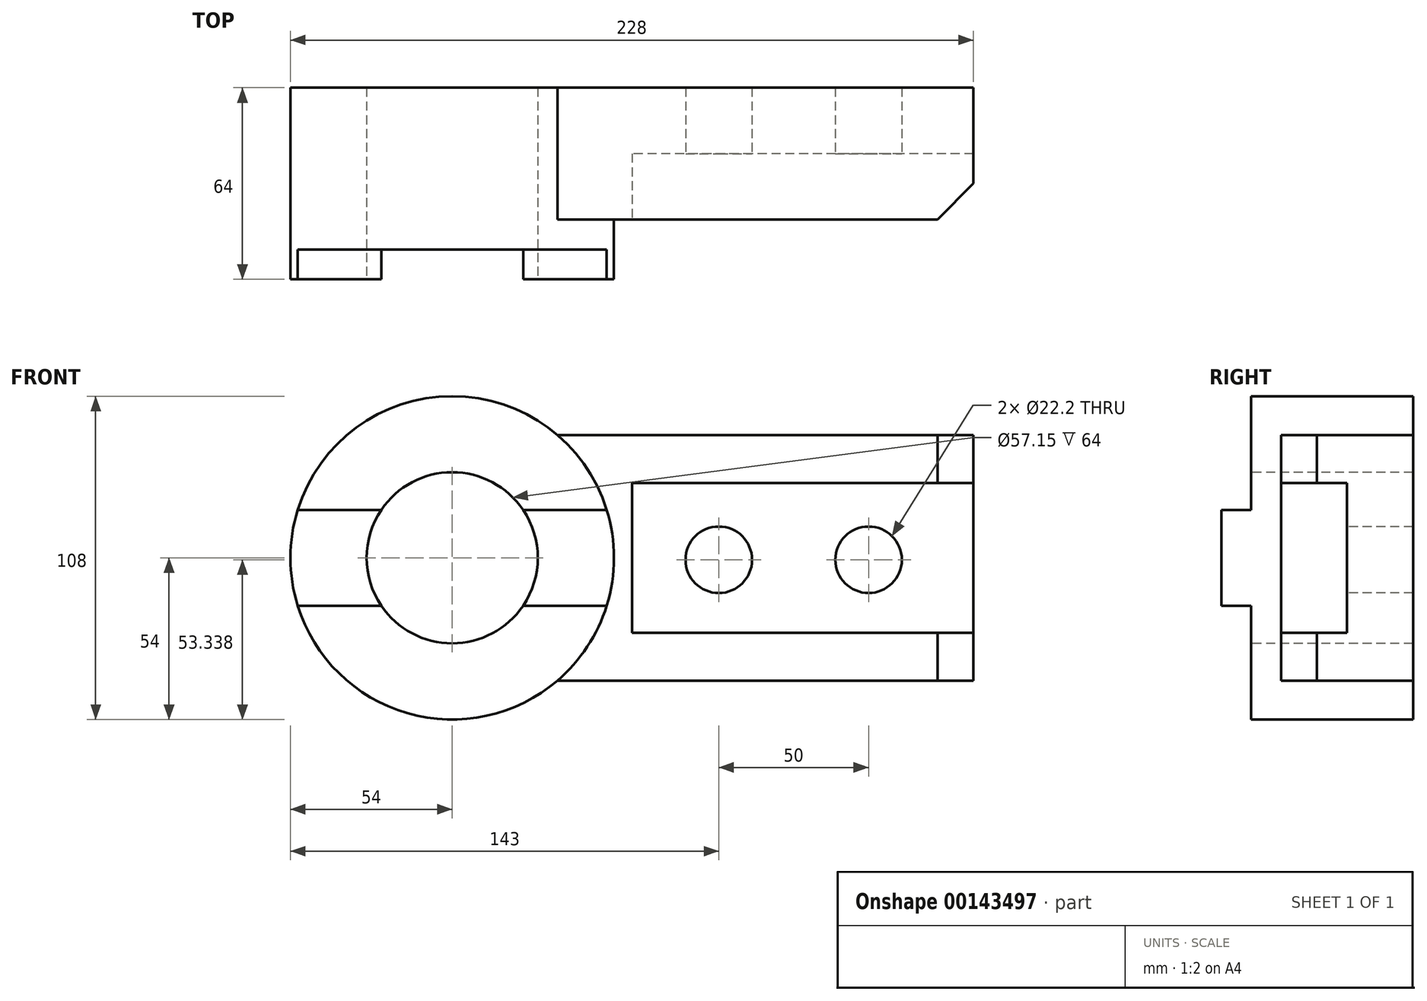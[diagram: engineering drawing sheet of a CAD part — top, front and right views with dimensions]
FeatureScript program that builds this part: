
annotation { "Feature Type Name" : "Feature", "Feature Type Description" : "" }
export const myFeature = defineFeature(function(context is Context, id is Id, definition is map)
    precondition{}
    {
        {
            var Q0;
            Q0=qCreatedBy(makeId("Front.planeOp"),FACE);
            var sketch = newSketch(context, id + "F0", { "sketchPlane" : qUnion([Q0])});
            skLineSegment(sketch, "E0.bottom", {"start": v(0, 0) * mm, "end": v(174, 0) * mm});
            skLineSegment(sketch, "E0.top", {"start": v(0, 82) * mm, "end": v(174, 82) * mm});
            skLineSegment(sketch, "E0.left", {"start": v(0, 0) * mm, "end": v(0, 82) * mm});
            skLineSegment(sketch, "E0.right", {"start": v(174, 0) * mm, "end": v(174, 82) * mm});
            skLineSegment(sketch, "E1.bottom", {"start": v(174, 66) * mm, "end": v(60, 66) * mm});
            skLineSegment(sketch, "E1.top", {"start": v(174, 16) * mm, "end": v(60, 16) * mm});
            skLineSegment(sketch, "E1.left", {"start": v(174, 66) * mm, "end": v(174, 16) * mm});
            skLineSegment(sketch, "E1.right", {"start": v(60, 66) * mm, "end": v(60, 16) * mm});
            skSolve(sketch);
        }
        {
            var Q0;
            {var subQ1=sQuery(id+"F0.wireOp",EDGE,"E0.bottom");Q0=makeQuery(id+"F0.imprint","IMPRINT",FACE,{"disambiguationData":[TD([[makeQuery(id+"F0.imprint","IMPRINT",EDGE,{"derivedFrom":subQ1}),1.0]])]});}
            var Q1;
            Q1=makeQuery(id+"F0.imprint","IMPRINT",FACE,{"disambiguationData":[TD([[makeQuery(id+"F0.imprint","IMPRINT",EDGE,{"derivedFrom":sQuery(id+"F0.wireOp",EDGE,"E1.bottom")}),1.0]])]});
            extrude(context, id + "F1", {"entities" : qUnion([Q0, Q1]), "oppositeDirection" : true, "depth" : 44 * mm});
        }
        {
            var Q0;
            Q0=makeQuery(id+"F0.imprint","IMPRINT",FACE,{"disambiguationData":[TD([[makeQuery(id+"F0.imprint","IMPRINT",EDGE,{"derivedFrom":sQuery(id+"F0.wireOp",EDGE,"E1.bottom")}),1.0]])]});
            extrude(context, id + "F2", {"entities" : qUnion([Q0]), "operationType" : NewBodyOperationType.REMOVE, "oppositeDirection" : true, "depth" : 22 * mm});
        }
        {
            var Q0;
            Q0=makeQuery(id+"F1.opExtrude","SWEPT_FACE",FACE,{"disambiguationData":[OSD([sQuery(id+"F0.wireOp",EDGE,"E0.top")])]});
            var sketch = newSketch(context, id + "F3", { "sketchPlane" : qUnion([Q0])});
            skLineSegment(sketch, "E2", {"start": v(174, 12) * mm, "end": v(162, 0) * mm});
            skLineSegment(sketch, "E3", {"start": v(162, 0) * mm, "end": v(174, 0) * mm});
            skLineSegment(sketch, "E4", {"start": v(174, 0) * mm, "end": v(174, 12) * mm});
            skSolve(sketch);
        }
        {
            var Q0;
            Q0 = qSketchRegion(id + "F3", true);
            extrude(context, id + "F4", {"entities" : qUnion([Q0]), "operationType" : NewBodyOperationType.REMOVE, "endBound" : BoundingType.THROUGH_ALL, "oppositeDirection" : true, "depth" : 25 * mm});
        }
        {
            var Q0;
            Q0=makeQuery(id+"F2.boolean.opBoolean","COPY",FACE,{"derivedFrom":makeQuery(id+"F2.opExtrude","CAP_FACE",FACE,{"disambiguationData":[OSD([sQuery(id+"F0.wireOp",EDGE,"E1.bottom"),sQuery(id+"F0.wireOp",EDGE,"E1.top"),sQuery(id+"F0.wireOp",EDGE,"E1.left"),sQuery(id+"F0.wireOp",EDGE,"E1.right")])],"isStart":false})});
            var sketch = newSketch(context, id + "F5", { "sketchPlane" : qUnion([Q0])});
            skPoint(sketch, "E5", {"position": v(89, 40.34) * mm});
            skPoint(sketch, "E6", {"position": v(139, 40.34) * mm});
            skSolve(sketch);
        }
        {
            var Q0;
            Q0=sQuery(id+"F5.wireOp",VERTEX,"E5");
            var Q1;
            Q1=sQuery(id+"F5.wireOp",VERTEX,"E6");
            var Q2;
            Q2=makeQuery(id+"F1.opExtrude","SWEPT_BODY",BODY,{"disambiguationData":[OSD([sQuery(id+"F0.wireOp",EDGE,"E0.bottom"),sQuery(id+"F0.wireOp",EDGE,"E0.top"),sQuery(id+"F0.wireOp",EDGE,"E0.left"),sQuery(id+"F0.wireOp",EDGE,"E0.right"),sQuery(id+"F0.wireOp",EDGE,"E1.left")])]});
            hole(context, id + "F6", {"style" : HoleStyle.SIMPLE, "endStyle" : HoleEndStyle.THROUGH, "holeDiameter" : 22.2 * mm, "locations" : qUnion([Q0, Q1]), "scope" : qUnion([Q2]), "isTappedThrough" : true});
        }
        {
            var Q0;
            Q0=qCreatedBy(makeId("Front.planeOp"),FACE);
            var sketch = newSketch(context, id + "F7", { "sketchPlane" : qUnion([Q0])});
            skLineSegment(sketch, "E7", {"start": v(0, 41) * mm, "end": v(181.48, 41) * mm, "construction": true});
            skLineSegment(sketch, "E8", {"start": v(0, 41) * mm, "end": v(0, 41) * mm});
            skCircle(sketch, "E9", {"center": v(0, 41) * mm, "radius": 54 * mm});
            skCircle(sketch, "E10", {"center": v(0, 41) * mm, "radius": 28.57 * mm});
            skSolve(sketch);
        }
        {
            var Q0;
            Q0=makeQuery(id+"F7.imprint","IMPRINT",FACE,{"disambiguationData":[TD([[makeQuery(id+"F7.imprint","IMPRINT",EDGE,{"derivedFrom":sQuery(id+"F7.wireOp",EDGE,"E9")}),1.0]])]});
            extrude(context, id + "F8", {"entities" : qUnion([Q0]), "operationType" : NewBodyOperationType.ADD, "oppositeDirection" : true, "depth" : 44 * mm, "hasSecondDirection" : true, "secondDirectionOppositeDirection" : false, "secondDirectionDepth" : 10 * mm});
        }
        {
            var Q0;
            {var subQ0=sQuery(id+"F0.wireOp",EDGE,"E0.left");Q0=makeQuery(id+"F8.boolean.opBoolean","SPLIT",FACE,{"disambiguationData":[TD([makeQuery(id+"F1.opExtrude","SWEPT_FACE",FACE,{"disambiguationData":[OSD([subQ0])]})])],"derivedFrom":makeQuery(id+"F1.opExtrude","CAP_FACE",FACE,{"disambiguationData":[OSD([sQuery(id+"F0.wireOp",EDGE,"E0.bottom"),sQuery(id+"F0.wireOp",EDGE,"E0.top"),subQ0,sQuery(id+"F0.wireOp",EDGE,"E0.right"),sQuery(id+"F0.wireOp",EDGE,"E1.left")])],"isStart":true})});}
            extrude(context, id + "F9", {"entities" : qUnion([Q0]), "operationType" : NewBodyOperationType.REMOVE, "endBound" : BoundingType.THROUGH_ALL, "oppositeDirection" : true, "depth" : 25 * mm});
        }
        {
            var Q0;
            Q0=makeQuery(id+"F8.opExtrude","CAP_FACE",FACE,{"disambiguationData":[OSD([sQuery(id+"F7.wireOp",EDGE,"E9"),sQuery(id+"F7.wireOp",EDGE,"E10")])],"isStart":true});
            var sketch = newSketch(context, id + "F10", { "sketchPlane" : qUnion([Q0])});
            skLineSegment(sketch, "E11", {"start": v(23.68, 57) * mm, "end": v(51.58, 57) * mm});
            skLineSegment(sketch, "E12", {"start": v(23.68, 25) * mm, "end": v(51.58, 25) * mm});
            skLineSegment(sketch, "E13", {"start": v(-23.68, 57) * mm, "end": v(-51.58, 57) * mm});
            skLineSegment(sketch, "E14", {"start": v(-23.68, 25) * mm, "end": v(-51.58, 25) * mm});
            skSolve(sketch);
        }
        {
            var Q0;
            {var subQ0=sQuery(id+"F10.wireOp",EDGE,"E11");Q0=makeQuery(id+"F10.imprint","IMPRINT",FACE,{"disambiguationData":[TD([[makeQuery(id+"F10.imprint","IMPRINT",EDGE,{"derivedFrom":subQ0}),-1.0]])]});}
            var Q1;
            {var subQ0=sQuery(id+"F10.wireOp",EDGE,"E13");Q1=makeQuery(id+"F10.imprint","IMPRINT",FACE,{"disambiguationData":[TD([[makeQuery(id+"F10.imprint","IMPRINT",EDGE,{"derivedFrom":subQ0}),1.0]])]});}
            extrude(context, id + "F11", {"entities" : qUnion([Q0, Q1]), "operationType" : NewBodyOperationType.ADD, "depth" : 10 * mm});
        }
    });
